# Revit family: PKSP
name_source: partatom
category: Lighting Fixtures
revit_build: Autodesk Revit Architecture 2012 (Build: 20110309_2315(x64)
units: mm (PartAtom-declared; Revit-internal decimal feet)

## types (13) — shared parameters
Apparent Load = 0 VA
Default Elevation = 48.000"
Description = The Parkway Square® wall sconce is a beautiful addition to both interior and exterior spaces. It is available in two scales for different mounting heights and can be mounted on a wall or column.
Lamp = LED
Light Bulb Material = Hubbell-Glass-Frosted
Load Classification = Lighting
Manufacturer = Architectural Area Lighting
Manufacturer Fax = (626)-369-2695
Model = Parkway Square Sconce-PKSP
Photometric Web = Web : PKSP-DB-70R111
Product Documentation Link = http://cdn.aal.net
Product Page URL = http://www.aal.net
URL = http://www.aal.net
Voltage = 120 V
Wattage Comments = 24W

## per-type parameters (varying)
| type | Finish |
| PKSP- ATG | Hubbell-Aluminum-Antique Green |
| PKSP- BLK | Hubbell-Aluminum-Black |
| PKSP- MTB | Hubbell-Aluminum-Matte Black |
| PKSP- DGN | Hubbell-Aluminum-Dark Green |
| PKSP- DBZ | Hubbell-Aluminum-Dark Bronze |
| PKSP- WRZ | Hubbell-Aluminum-Weathered Bronze |
| PKSP- BRM | Hubbell-Aluminum-Metalic Bronze |
| PKSP- VBL | Hubbell-Aluminum-Verde Blue |
| PKSP- CRT | Hubbell-Aluminum-Corten |
| PKSP- MAL | Hubbell-Aluminum-Matte |
| PKSP- MDG | Hubbell-Aluminum-Medium Grey |
| PKSP- LGY | Hubbell-Aluminum-Light Grey |
| PKSP- AWT | Hubbell-Aluminum-Artic White |

## geometry (parser evidence)
native form markers: Blend x12, Sweep x6
no freeform markers — native parametric forms only
